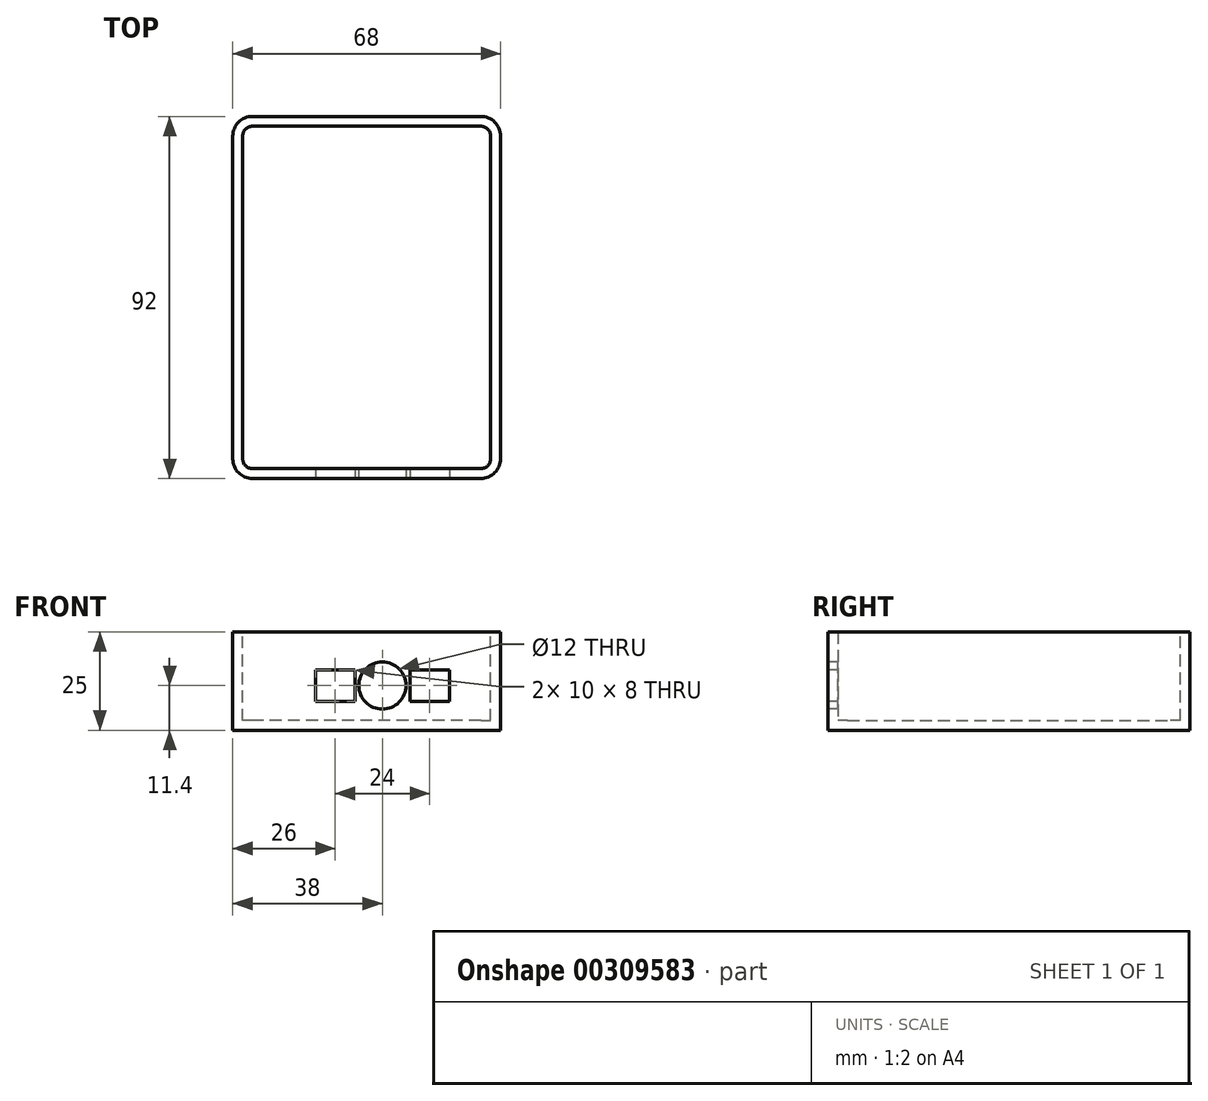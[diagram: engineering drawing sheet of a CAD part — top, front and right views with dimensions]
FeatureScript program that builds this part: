
annotation { "Feature Type Name" : "Feature", "Feature Type Description" : "" }
export const myFeature = defineFeature(function(context is Context, id is Id, definition is map)
    precondition{}
    {
        {
            var Q0;
            Q0=qCreatedBy(makeId("Top.planeOp"),FACE);
            var sketch = newSketch(context, id + "F0", { "sketchPlane" : qUnion([Q0])});
            skLineSegment(sketch, "E0.bottom", {"start": v(0, 0) * mm, "end": v(58, 0) * mm});
            skLineSegment(sketch, "E0.top", {"start": v(0, 82) * mm, "end": v(58, 82) * mm});
            skLineSegment(sketch, "E0.left", {"start": v(0, 0) * mm, "end": v(0, 82) * mm});
            skLineSegment(sketch, "E0.right", {"start": v(58, 0) * mm, "end": v(58, 82) * mm});
            skSolve(sketch);
        }
        {
            var Q0;
            Q0=makeQuery(id+"F0.imprint","IMPRINT",FACE,{"disambiguationData":[TD([[makeQuery(id+"F0.imprint","IMPRINT",EDGE,{"derivedFrom":sQuery(id+"F0.wireOp",EDGE,"E0.bottom")}),1.0]])]});
            extrude(context, id + "F1", {"entities" : qUnion([Q0]), "depth" : 19 * mm, "offsetDistance" : 25 * mm});
        }
        {
            var Q0;
            Q0=qCreatedBy(makeId("Top.planeOp"),FACE);
            var sketch = newSketch(context, id + "F2", { "sketchPlane" : qUnion([Q0])});
            skLineSegment(sketch, "E1.0.0", {"start": v(58, 82) * mm, "end": v(0, 82) * mm, "construction": true});
            skLineSegment(sketch, "E1.0.1", {"start": v(0, 82) * mm, "end": v(0, 0) * mm, "construction": true});
            skLineSegment(sketch, "E1.0.2", {"start": v(0, 0) * mm, "end": v(58, 0) * mm, "construction": true});
            skLineSegment(sketch, "E1.0.3", {"start": v(58, 0) * mm, "end": v(58, 82) * mm, "construction": true});
            skLineSegment(sketch, "E2.0", {"start": v(-5, 87) * mm, "end": v(63, 87) * mm});
            skLineSegment(sketch, "E2.1", {"start": v(-5, -5) * mm, "end": v(-5, 87) * mm});
            skLineSegment(sketch, "E2.2", {"start": v(63, -5) * mm, "end": v(-5, -5) * mm});
            skLineSegment(sketch, "E2.3", {"start": v(63, 87) * mm, "end": v(63, -5) * mm});
            skSolve(sketch);
        }
        {
            var Q0;
            Q0 = qSketchRegion(id + "F2", true);
            extrude(context, id + "F3", {"entities" : qUnion([Q0]), "depth" : 25 * mm, "offsetDistance" : 25 * mm});
        }
        {
            var Q0;
            Q0=makeQuery(id+"F3.opExtrude","SWEPT_EDGE",EDGE,{"disambiguationData":[OSD([sQuery(id+"F2.wireOp",EDGE,"E2.1"),sQuery(id+"F2.wireOp",EDGE,"E2.2")])]});
            var Q1;
            Q1=makeQuery(id+"F3.opExtrude","SWEPT_EDGE",EDGE,{"disambiguationData":[OSD([sQuery(id+"F2.wireOp",EDGE,"E2.2"),sQuery(id+"F2.wireOp",EDGE,"E2.3")])]});
            var Q2;
            Q2=makeQuery(id+"F3.opExtrude","SWEPT_EDGE",EDGE,{"disambiguationData":[OSD([sQuery(id+"F2.wireOp",EDGE,"E2.0"),sQuery(id+"F2.wireOp",EDGE,"E2.1")])]});
            var Q3;
            Q3=makeQuery(id+"F3.opExtrude","SWEPT_EDGE",EDGE,{"disambiguationData":[OSD([sQuery(id+"F2.wireOp",EDGE,"E2.0"),sQuery(id+"F2.wireOp",EDGE,"E2.3")])]});
            fillet(context, id + "F4", {"entities" : qUnion([Q0, Q1, Q2, Q3]), "radius" : 5 * mm, "tangentPropagation" : true, "allowEdgeOverflow" : false});
        }
        {
            var Q0;
            Q0=makeQuery(id+"F3.opExtrude","CAP_FACE",FACE,{"disambiguationData":[OSD([sQuery(id+"F2.wireOp",EDGE,"E2.0"),sQuery(id+"F2.wireOp",EDGE,"E2.1"),sQuery(id+"F2.wireOp",EDGE,"E2.2"),sQuery(id+"F2.wireOp",EDGE,"E2.3")])],"isStart":false});
            shell(context, id + "F5", {"entities" : qUnion([Q0]), "thickness" : 2.5 * mm});
        }
        {
            var Q0;
            Q0=makeQuery(id+"F3.opExtrude","SWEPT_FACE",FACE,{"disambiguationData":[OSD([sQuery(id+"F2.wireOp",EDGE,"E2.2")])]});
            var sketch = newSketch(context, id + "F6", { "sketchPlane" : qUnion([Q0])});
            skLineSegment(sketch, "E3.bottom", {"start": v(16, 15.4) * mm, "end": v(26, 15.4) * mm});
            skLineSegment(sketch, "E3.top", {"start": v(16, 7.4) * mm, "end": v(26, 7.4) * mm});
            skLineSegment(sketch, "E3.left", {"start": v(16, 15.4) * mm, "end": v(16, 7.4) * mm});
            skLineSegment(sketch, "E3.right", {"start": v(26, 15.4) * mm, "end": v(26, 7.4) * mm});
            skLineSegment(sketch, "E4.bottom", {"start": v(40, 15.4) * mm, "end": v(50, 15.4) * mm});
            skLineSegment(sketch, "E4.top", {"start": v(40, 7.4) * mm, "end": v(50, 7.4) * mm});
            skLineSegment(sketch, "E4.left", {"start": v(40, 15.4) * mm, "end": v(40, 7.4) * mm});
            skLineSegment(sketch, "E4.right", {"start": v(50, 15.4) * mm, "end": v(50, 7.4) * mm});
            skCircle(sketch, "E5", {"center": v(33, 11.4) * mm, "radius": 6 * mm});
            skPoint(sketch, "E5.centerSnap0", {"position": v(26, 11.4) * mm});
            skSolve(sketch);
        }
        {
            var Q0;
            Q0=makeQuery(id+"F6.imprint","IMPRINT",FACE,{"disambiguationData":[TD([[makeQuery(id+"F6.imprint","IMPRINT",EDGE,{"derivedFrom":sQuery(id+"F6.wireOp",EDGE,"E3.bottom")}),-1.0]])]});
            var Q1;
            Q1=makeQuery(id+"F6.imprint","IMPRINT",FACE,{"disambiguationData":[TD([[makeQuery(id+"F6.imprint","IMPRINT",EDGE,{"derivedFrom":sQuery(id+"F6.wireOp",EDGE,"E5")}),1.0]])]});
            var Q2;
            Q2=makeQuery(id+"F6.imprint","IMPRINT",FACE,{"disambiguationData":[TD([[makeQuery(id+"F6.imprint","IMPRINT",EDGE,{"derivedFrom":sQuery(id+"F6.wireOp",EDGE,"E4.bottom")}),-1.0]])]});
            extrude(context, id + "F7", {"entities" : qUnion([Q0, Q1, Q2]), "operationType" : NewBodyOperationType.REMOVE, "oppositeDirection" : true, "depth" : 25 * mm, "offsetDistance" : 25 * mm});
        }
        {
            var Q0;
            Q0=makeQuery(id+"F1.opExtrude","SWEPT_BODY",BODY,{"disambiguationData":[OSD([sQuery(id+"F0.wireOp",EDGE,"E0.bottom"),sQuery(id+"F0.wireOp",EDGE,"E0.top"),sQuery(id+"F0.wireOp",EDGE,"E0.left"),sQuery(id+"F0.wireOp",EDGE,"E0.right")])]});
            deleteBodies(context, id + "F8", {"entities" : qUnion([Q0])});
        }
    });
